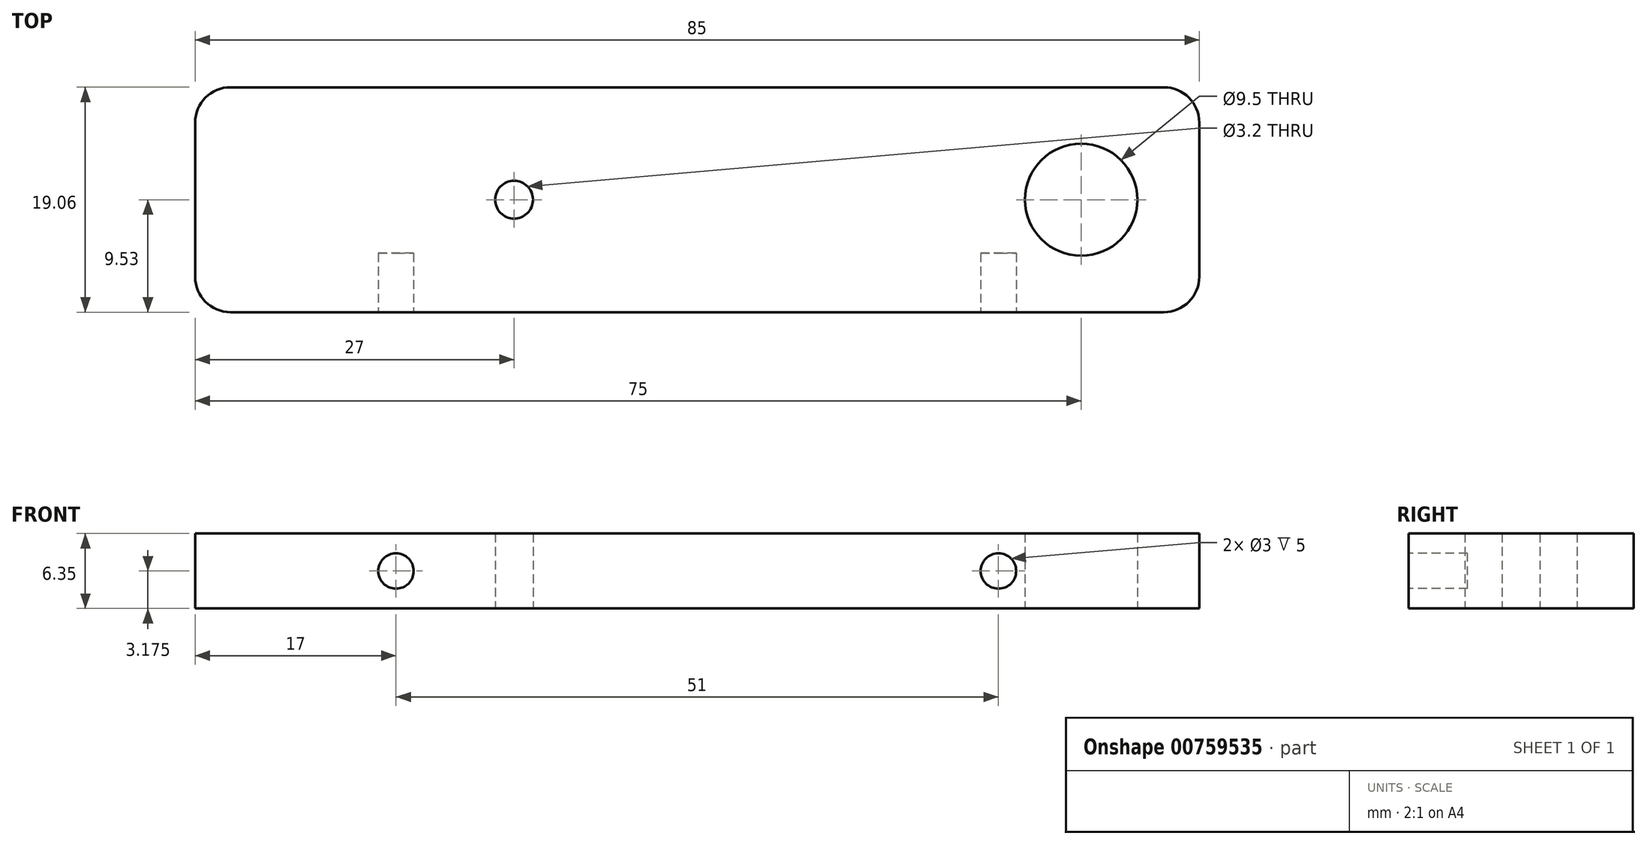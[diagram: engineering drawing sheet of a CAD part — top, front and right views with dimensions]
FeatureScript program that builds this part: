
annotation { "Feature Type Name" : "Feature", "Feature Type Description" : "" }
export const myFeature = defineFeature(function(context is Context, id is Id, definition is map)
    precondition{}
    {
        {
            var Q0;
            Q0=qCreatedBy(makeId("Top.planeOp"),FACE);
            var sketch = newSketch(context, id + "F0", { "sketchPlane" : qUnion([Q0])});
            skLineSegment(sketch, "E0.bottom", {"start": v(39.5, 9.53) * mm, "end": v(-39.5, 9.53) * mm});
            skLineSegment(sketch, "E0.top", {"start": v(39.5, -9.53) * mm, "end": v(-39.5, -9.53) * mm});
            skLineSegment(sketch, "E0.left", {"start": v(42.5, 6.53) * mm, "end": v(42.5, -6.53) * mm});
            skLineSegment(sketch, "E0.right", {"start": v(-42.5, 6.53) * mm, "end": v(-42.5, -6.53) * mm});
            skPoint(sketch, "E0.middle", {"position": v(0, 0) * mm});
            skCircle(sketch, "E1", {"center": v(32.5, 0) * mm, "radius": 4.75 * mm});
            skCircle(sketch, "E2", {"center": v(-15.5, 0) * mm, "radius": 1.6 * mm});
            skPoint(sketch, "E3.visualSharp", {"position": v(-42.5, 9.53) * mm});
            skArc(sketch, "E3.filletArc", {"start": v(-39.5, 9.53) * mm, "mid": v(-41.62, 8.65) * mm, "end": v(-42.5, 6.53) * mm});
            skPoint(sketch, "E4.visualSharp", {"position": v(-42.5, -9.53) * mm});
            skArc(sketch, "E4.filletArc", {"start": v(-42.5, -6.53) * mm, "mid": v(-41.62, -8.65) * mm, "end": v(-39.5, -9.53) * mm});
            skPoint(sketch, "E5.visualSharp", {"position": v(42.5, 9.53) * mm});
            skArc(sketch, "E5.filletArc", {"start": v(42.5, 6.53) * mm, "mid": v(41.62, 8.65) * mm, "end": v(39.5, 9.53) * mm});
            skPoint(sketch, "E6.visualSharp", {"position": v(42.5, -9.53) * mm});
            skArc(sketch, "E6.filletArc", {"start": v(39.5, -9.53) * mm, "mid": v(41.62, -8.65) * mm, "end": v(42.5, -6.53) * mm});
            skSolve(sketch);
        }
        {
            var Q0;
            Q0 = qSketchRegion(id + "F0", true);
            extrude(context, id + "F1", {"entities" : qUnion([Q0]), "depth" : 6.35 * mm, "offsetDistance" : 25 * mm});
        }
        {
            var Q0;
            Q0=makeQuery(id+"F1.opExtrude","SWEPT_FACE",FACE,{"disambiguationData":[OSD([sQuery(id+"F0.wireOp",EDGE,"E0.top")])]});
            var sketch = newSketch(context, id + "F2", { "sketchPlane" : qUnion([Q0])});
            skCircle(sketch, "E7", {"center": v(-25.5, 3.18) * mm, "radius": 1.5 * mm});
            skPoint(sketch, "E7.centerSnap0", {"position": v(-39.5, 3.17) * mm});
            skCircle(sketch, "E8.MirrorC", {"center": v(25.5, 3.18) * mm, "radius": 1.5 * mm});
            skSolve(sketch);
        }
        {
            var Q0;
            Q0 = qSketchRegion(id + "F2", true);
            extrude(context, id + "F3", {"entities" : qUnion([Q0]), "operationType" : NewBodyOperationType.REMOVE, "oppositeDirection" : true, "depth" : 5 * mm, "offsetDistance" : 25 * mm});
        }
    });
